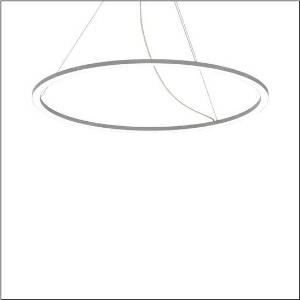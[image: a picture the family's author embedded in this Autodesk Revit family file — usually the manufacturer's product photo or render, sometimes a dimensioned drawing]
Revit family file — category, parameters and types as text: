
# Revit family: silica_21_ring-d_5pjbd4d1204a
name_source: partatom
category: Lighting Fixtures
units: mm (PartAtom-declared; Revit-internal decimal feet)

## family parameters
Cut with Voids When Loaded = No
Host = Face
Light Source = No
Part Type = Normal
Room Calculation Point = No
Round Connector Dimension = Use Diameter
Shared = No

## types (1)
- Silica 21 Ring-D (1 x LED, 10840 lm, 125 W, 3000K)
    Apparent Load = 125 VA
    CIE Flux Codes = 37 69 92 100 100
    Color Rendering = 80
    Color Temperature = 3000K
    Default Elevation = 1800 mm
    Description = Silica 21 Ring-D, suspended luminaire, of PMMA, frosted, light emission: ring underside luminous distribution, primary light characteristic: symmetric, installation type: suspended mounting, LED, rated luminous flux: 10.840lm, luminous efficacy: 87lm/W, light colour: 830, colour temperature: 3000K, control gear: DALI 2, with terminal, 5-pole, mains connection: 230V, AC/DC, 0/50..60Hz, rated input power: 125W, housing, of extruded aluminium section, metallic grey (RAL 9006), diameter: 1.450mm, ceiling canopy, metallic grey (RAL 9006), protection rating (lamp compartment): IP40, insulation class (complete): insulation class I (protective earthing), certification: CE, impact resistance: IK02, permissible operating ambient temperature: 0..+35°C, packaging unit: 1 piece
    Height = 25 mm  [stored 0.082021 ft]
    Lamp = 1 x LED
    Lamp Light Flux = 10840 lm
    Lamp Power = 125 W
    Lamp count = 1
    Length = 1450 mm
    Luminous efficacy = 87 lm/W
    Manufacturer = Siteco
    ModVariant = No
    Model = 5PJBD4D1204A
    Mounting Place = Ceiling
    Mounting Type = Pendant
    Number of Poles = 1
    OnlyDefault = Yes
    Power Factor = 1
    Product Name = Silica 21 Ring-D
    Product group = suspended luminaire
    ProductGroupID = 904
    Protection Class = Protection class I
    Protection Degree = IP 40
    RLX_Detail_Level = 1
    RLX_Emergency_Light_Flux = 0 lm
    RLX_Emergency_Type = 0
    RLX_Emergency_Type_DB = No
    RlxData = <blob elided: 17925 chars, md5=1a434d21>
    Socket = socket
    Standby Power = 0 W
    System Light Flux = 10840 lm
    System Power = 125 W
    Type Comments = Product without accessories
    Type Image = l_1251748.jpg
    URL = http://relux.com
    VarID = ---
    Voltage = 0 V
    Weight = 0.00 kg
    Width = 0 mm  [stored 0 ft]

note: [stored X ft] marks values corroborated as IEEE doubles in the binary element streams (Revit-internal decimal feet)

## geometry (parser evidence)
native form markers: Blend x4, Sweep x9
no freeform markers — native parametric forms only
